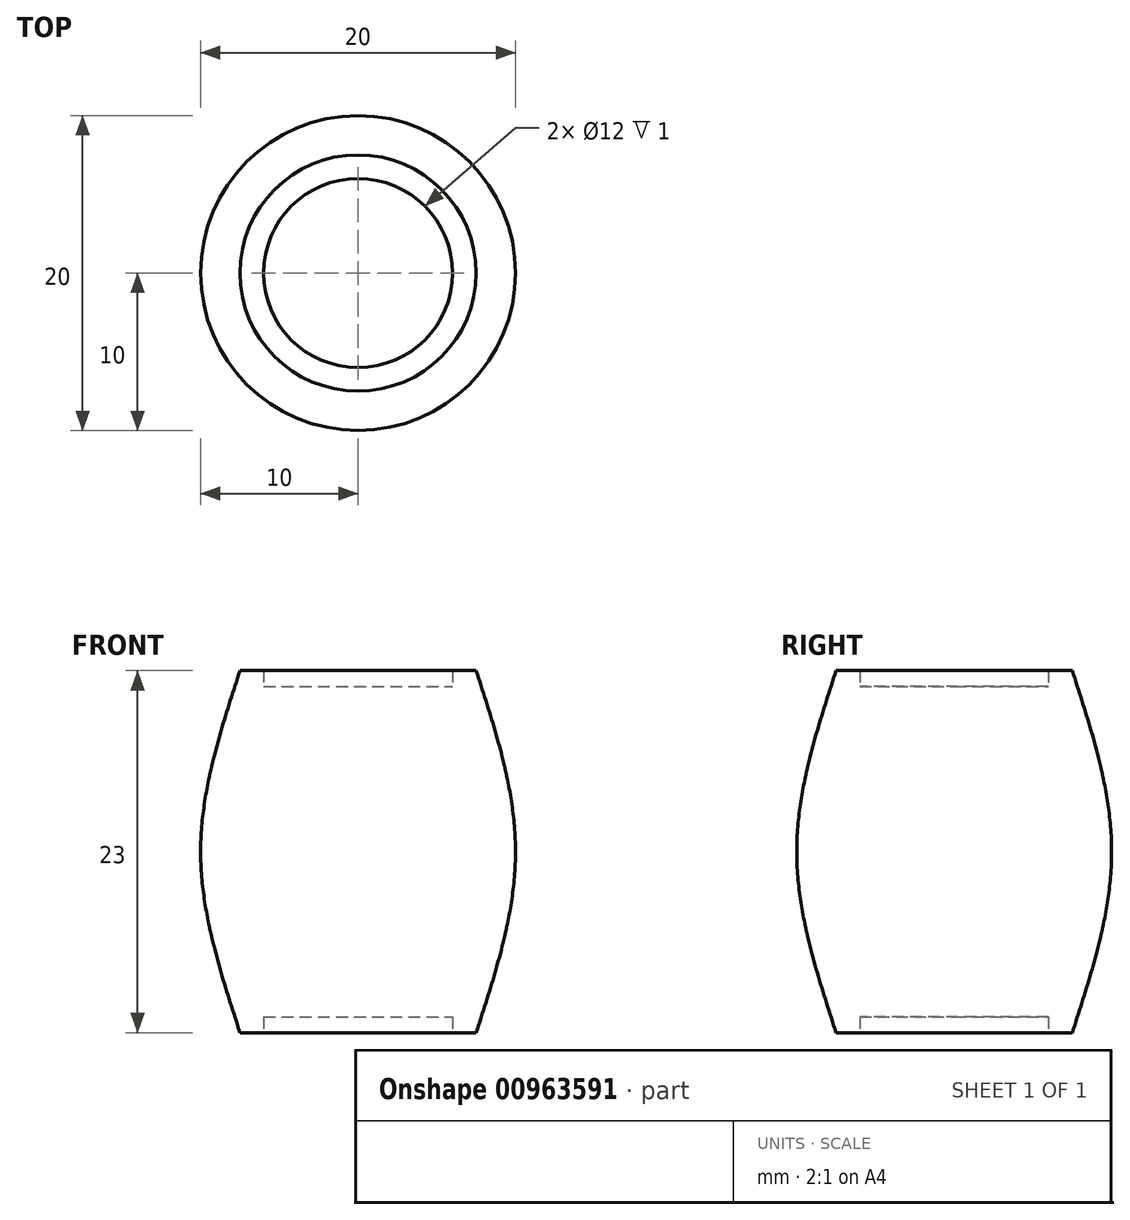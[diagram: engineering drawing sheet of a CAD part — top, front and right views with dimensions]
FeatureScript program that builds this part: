
annotation { "Feature Type Name" : "Feature", "Feature Type Description" : "" }
export const myFeature = defineFeature(function(context is Context, id is Id, definition is map)
    precondition{}
    {
        {
            var Q0;
            Q0=qCreatedBy(makeId("Front.planeOp"),FACE);
            var sketch = newSketch(context, id + "F0", { "sketchPlane" : qUnion([Q0])});
            skLineSegment(sketch, "E0", {"start": v(0, 1) * mm, "end": v(0, 22) * mm});
            skLineSegment(sketch, "E1", {"start": v(-6, 23) * mm, "end": v(-7.5, 23) * mm});
            skLineSegment(sketch, "E2", {"start": v(-6, 0) * mm, "end": v(-7.5, 0) * mm});
            skLineSegment(sketch, "E3", {"start": v(0, 11.5) * mm, "end": v(-10, 11.5) * mm});
            skFitSpline(sketch, "E4", {"points": [v(-7.5, 23) * mm, v(-10, 11.5) * mm, v(-7.5, 0) * mm], "startDerivative": vector(-7.5, -23) * mm, "endDerivative": vector(7.5, -23) * mm});
            skLineSegment(sketch, "E5", {"start": v(0, 22) * mm, "end": v(-6, 22) * mm});
            skLineSegment(sketch, "E6", {"start": v(-6, 1) * mm, "end": v(0, 1) * mm});
            skLineSegment(sketch, "E7", {"start": v(-6, 23) * mm, "end": v(-6, 22) * mm});
            skPoint(sketch, "E8.orphan", {"position": v(0, 23) * mm});
            skLineSegment(sketch, "E9.trimOffspring", {"start": v(-6, 1) * mm, "end": v(-6, 0) * mm});
            skPoint(sketch, "E10.orphan", {"position": v(0, 0) * mm});
            skFitSpline(sketch, "E11.0", {"points": [v(-8.12, 23.2) * mm, v(-8.43, 22.24) * mm, v(-9.06, 20.32) * mm, v(-9.89, 17.4) * mm, v(-10.39, 14.96) * mm, v(-10.6, 12.99) * mm, v(-10.67, 11.5) * mm, v(-10.6, 10.01) * mm, v(-10.39, 8.04) * mm, v(-9.89, 5.6) * mm, v(-9.06, 2.68) * mm, v(-8.43, 0.76) * mm, v(-8.12, -0.2) * mm]});
            skLineSegment(sketch, "E12.bottom", {"start": v(-9.16, 17.5) * mm, "end": v(-9.83, 17.5) * mm});
            skLineSegment(sketch, "E12.top", {"start": v(-9.48, 16.1) * mm, "end": v(-10.14, 16.1) * mm});
            skLineSegment(sketch, "E13.bottom", {"start": v(-10.14, 6.9) * mm, "end": v(-9.48, 6.9) * mm});
            skLineSegment(sketch, "E13.top", {"start": v(-9.83, 5.5) * mm, "end": v(-9.16, 5.5) * mm});
            skFitSpline(sketch, "E14.trimOffspring", {"points": [v(-8.12, 23.2) * mm, v(-8.43, 22.24) * mm, v(-9.06, 20.32) * mm, v(-9.89, 17.4) * mm, v(-10.39, 14.96) * mm, v(-10.6, 12.99) * mm, v(-10.67, 11.5) * mm, v(-10.6, 10.01) * mm, v(-10.39, 8.04) * mm, v(-9.89, 5.6) * mm, v(-9.06, 2.68) * mm, v(-8.43, 0.76) * mm, v(-8.12, -0.2) * mm]});
            skSolve(sketch);
        }
        {
            var Q0;
            Q0=qSketchRegion(id+"F0",true);
            var Q1;
            Q1=sQuery(id+"F0.wireOp",EDGE,"E0");
            revolve(context, id + "F1", {"surfaceOperationType" : NewSurfaceOperationType.NEW, "entities" : qUnion([Q0]), "axis" : qUnion([Q1]), "revolveType" : RevolveType.FULL});
        }
    });
